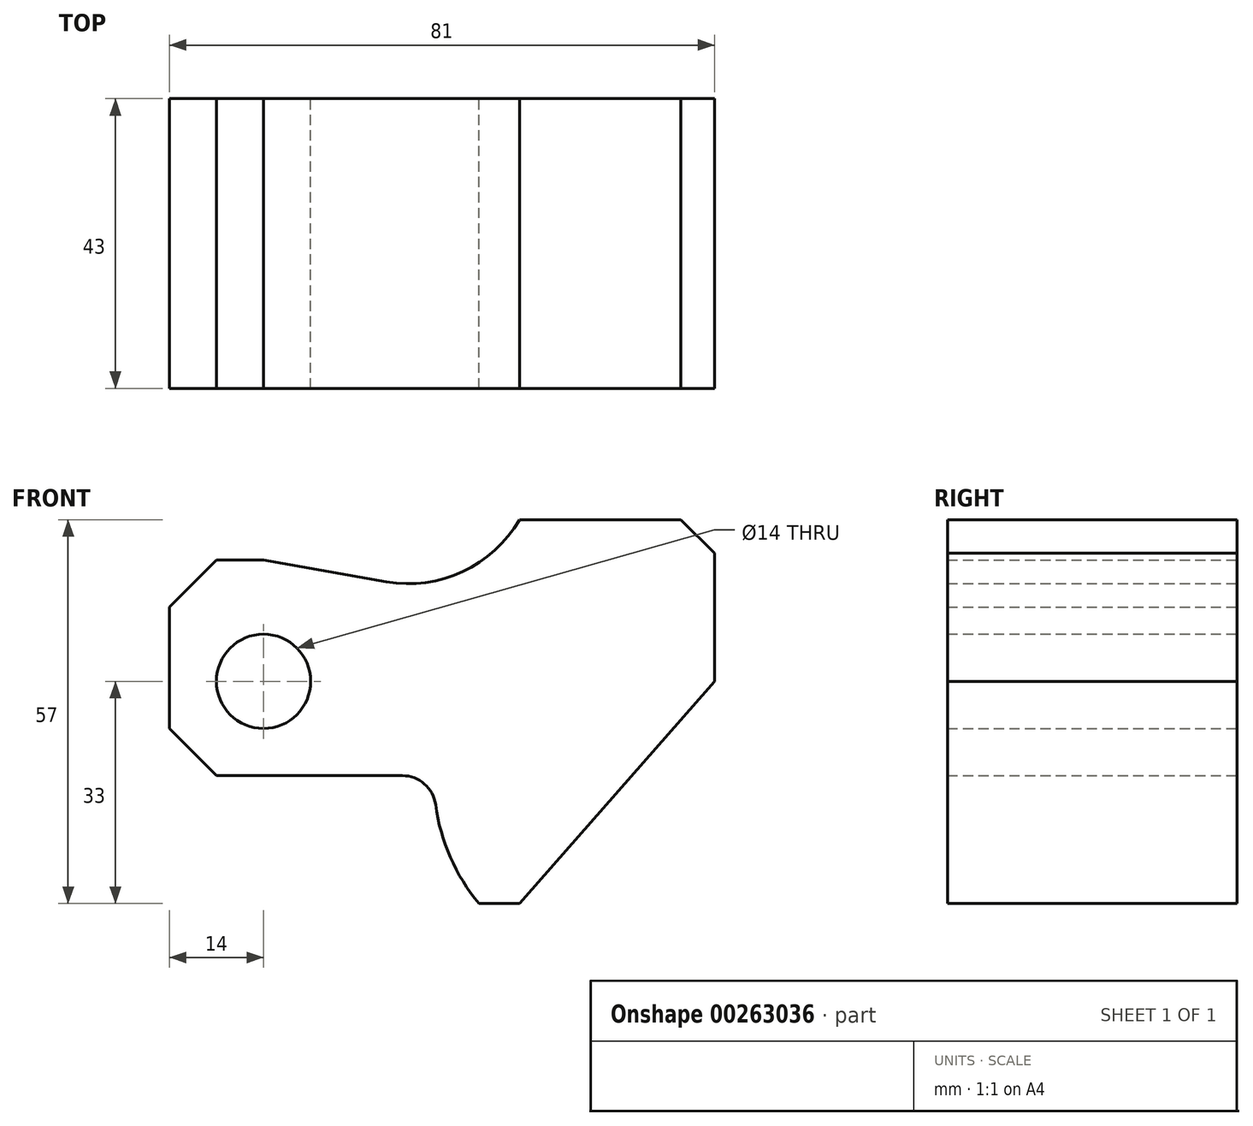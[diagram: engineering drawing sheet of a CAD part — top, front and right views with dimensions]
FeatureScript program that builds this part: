
annotation { "Feature Type Name" : "Feature", "Feature Type Description" : "" }
export const myFeature = defineFeature(function(context is Context, id is Id, definition is map)
    precondition{}
    {
        {
            var Q0;
            Q0=qCreatedBy(makeId("Front.planeOp"),FACE);
            var sketch = newSketch(context, id + "F0", { "sketchPlane" : qUnion([Q0])});
            skCircle(sketch, "E0", {"center": v(0, 0) * mm, "radius": 7 * mm});
            skLineSegment(sketch, "E1", {"start": v(-14, -7) * mm, "end": v(-7, -14) * mm});
            skLineSegment(sketch, "E2", {"start": v(-14, 11) * mm, "end": v(-7, 18) * mm});
            skLineSegment(sketch, "E3", {"start": v(-7, -14) * mm, "end": v(20.6, -14) * mm});
            skLineSegment(sketch, "E4", {"start": v(-7, 18) * mm, "end": v(0, 18) * mm});
            skLineSegment(sketch, "E5", {"start": v(0, 18) * mm, "end": v(18.24, 14.78) * mm});
            skLineSegment(sketch, "E6", {"start": v(62, 24) * mm, "end": v(67, 19) * mm});
            skLineSegment(sketch, "E7", {"start": v(67, 19) * mm, "end": v(67, 0) * mm});
            skLineSegment(sketch, "E8", {"start": v(67, 0) * mm, "end": v(38, -33) * mm});
            skLineSegment(sketch, "E9", {"start": v(32, -33) * mm, "end": v(38, -33) * mm});
            skArc(sketch, "E10", {"start": v(25.56, -18.33) * mm, "mid": v(23.9, -15.24) * mm, "end": v(20.6, -14) * mm});
            skArc(sketch, "E11", {"start": v(25.56, -18.33) * mm, "mid": v(27.75, -26.12) * mm, "end": v(32, -33) * mm});
            skLineSegment(sketch, "E12", {"start": v(-14, -7) * mm, "end": v(-14, 11) * mm});
            skLineSegment(sketch, "E13", {"start": v(-14, 11) * mm, "end": v(-14, 18) * mm, "construction": true});
            skLineSegment(sketch, "E14", {"start": v(-14, -7) * mm, "end": v(-14, -14.36) * mm, "construction": true});
            skArc(sketch, "E15", {"start": v(18.24, 14.78) * mm, "mid": v(29.57, 16.28) * mm, "end": v(38, 24) * mm});
            skLineSegment(sketch, "E16", {"start": v(38, 24) * mm, "end": v(62, 24) * mm});
            skSolve(sketch);
        }
        {
            var Q0;
            Q0 = qSketchRegion(id + "F0", true);
            extrude(context, id + "F1", {"entities" : qUnion([Q0]), "endBound" : BoundingType.SYMMETRIC, "depth" : 43 * mm});
        }
    });
